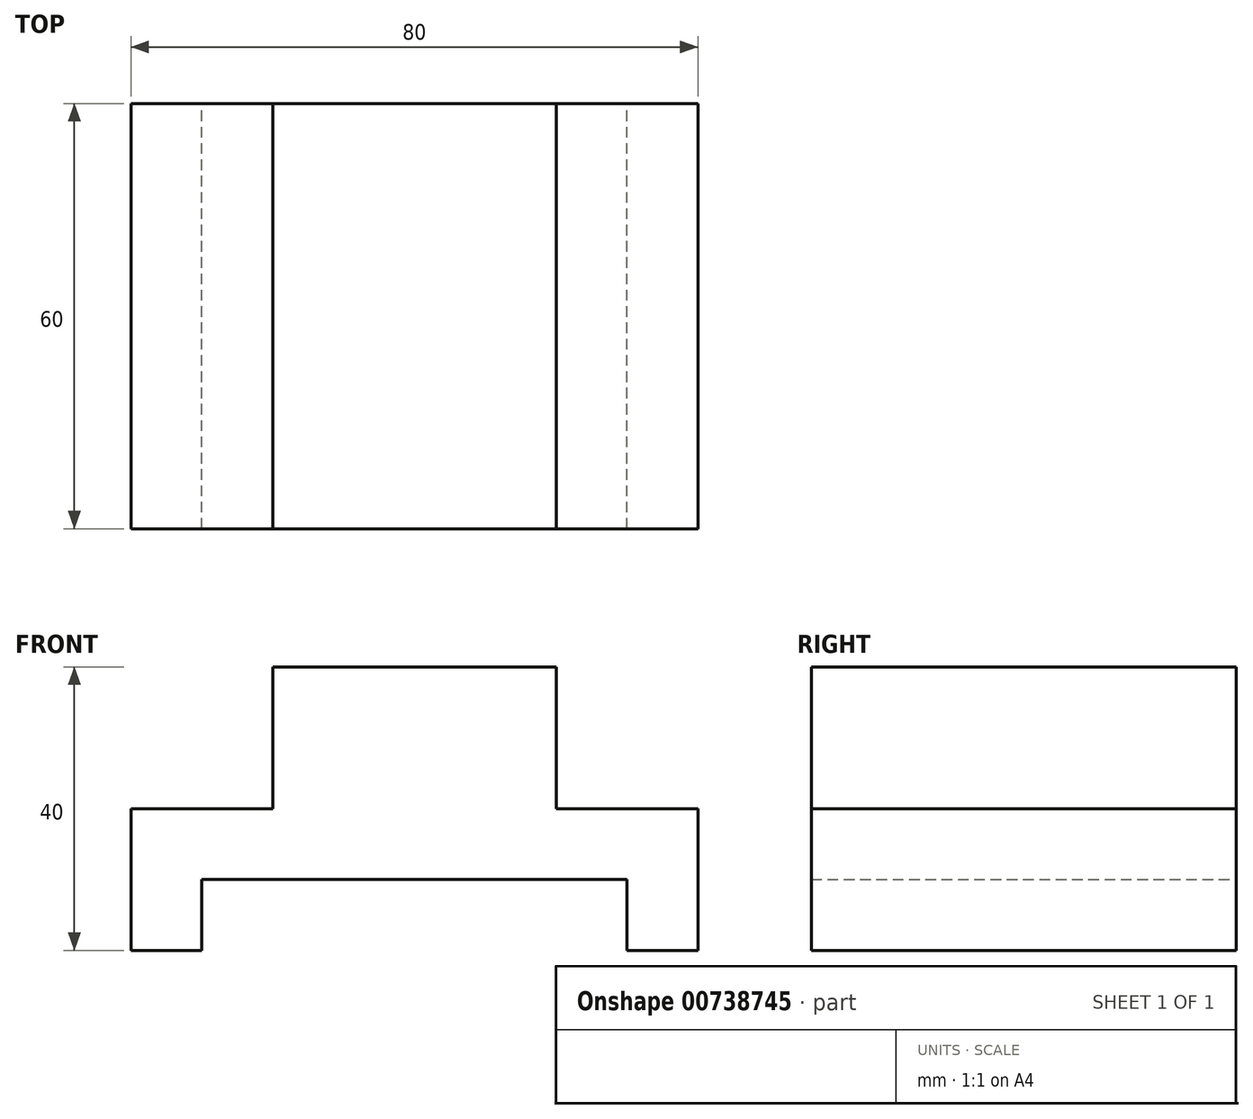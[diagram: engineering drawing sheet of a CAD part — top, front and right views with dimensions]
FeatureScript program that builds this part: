
annotation { "Feature Type Name" : "Feature", "Feature Type Description" : "" }
export const myFeature = defineFeature(function(context is Context, id is Id, definition is map)
    precondition{}
    {
        {
            var Q0;
            Q0=qCreatedBy(makeId("Front.planeOp"),FACE);
            var sketch = newSketch(context, id + "F0", { "sketchPlane" : qUnion([Q0])});
            skLineSegment(sketch, "E0", {"start": v(0, 0) * mm, "end": v(0, 20) * mm});
            skLineSegment(sketch, "E1", {"start": v(0, 20) * mm, "end": v(20, 20) * mm});
            skLineSegment(sketch, "E2", {"start": v(20, 20) * mm, "end": v(20, 40) * mm});
            skLineSegment(sketch, "E3", {"start": v(20, 40) * mm, "end": v(60, 40) * mm});
            skLineSegment(sketch, "E4", {"start": v(0, 10) * mm, "end": v(0, 0) * mm});
            skLineSegment(sketch, "E5", {"start": v(0, 0) * mm, "end": v(10, 0) * mm});
            skLineSegment(sketch, "E6", {"start": v(10, 0) * mm, "end": v(10, 10) * mm});
            skLineSegment(sketch, "E7", {"start": v(40, 40) * mm, "end": v(40, 0) * mm, "construction": true});
            skLineSegment(sketch, "E8.MirrorCS", {"start": v(60, 20) * mm, "end": v(60, 40) * mm});
            skLineSegment(sketch, "E9.MirrorCS", {"start": v(80, 20) * mm, "end": v(60, 20) * mm});
            skLineSegment(sketch, "E10.MirrorCS", {"start": v(80, 0) * mm, "end": v(80, 20) * mm});
            skLineSegment(sketch, "E11.MirrorCS", {"start": v(80, 0) * mm, "end": v(70, 0) * mm});
            skLineSegment(sketch, "E12.MirrorCS", {"start": v(70, 0) * mm, "end": v(70, 10) * mm});
            skLineSegment(sketch, "E13", {"start": v(10, 10) * mm, "end": v(70, 10) * mm});
            skSolve(sketch);
        }
        {
            var Q0;
            Q0=makeQuery(id+"F0.imprint","IMPRINT",FACE,{"disambiguationData":[TD([[makeQuery(id+"F0.imprint","IMPRINT",EDGE,{"derivedFrom":sQuery(id+"F0.wireOp",EDGE,"E0")}),-1.0]])]});
            extrude(context, id + "F1", {"entities" : qUnion([Q0]), "endBound" : BoundingType.SYMMETRIC, "depth" : 60 * mm, "offsetDistance" : 25 * mm});
        }
    });
